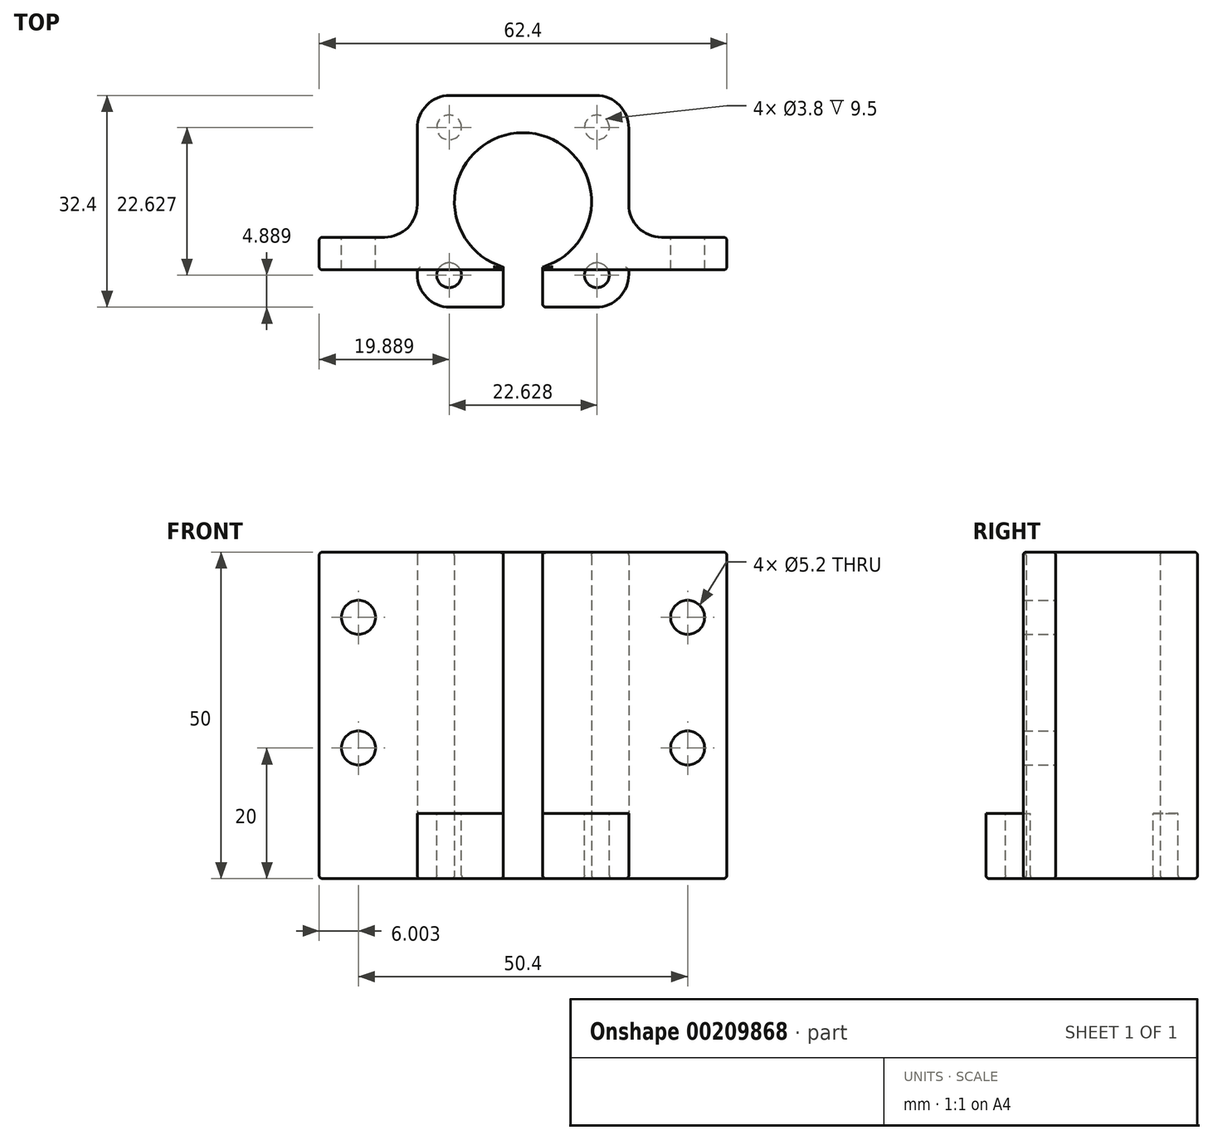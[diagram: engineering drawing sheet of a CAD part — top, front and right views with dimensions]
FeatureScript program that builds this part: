
annotation { "Feature Type Name" : "Feature", "Feature Type Description" : "" }
export const myFeature = defineFeature(function(context is Context, id is Id, definition is map)
    precondition{}
    {
        {
            var Q0;
            Q0=qCreatedBy(makeId("Top.planeOp"),FACE);
            var sketch = newSketch(context, id + "F0", { "sketchPlane" : qUnion([Q0])});
            skCircle(sketch, "E0", {"center": v(-42.16, 28.22) * mm, "radius": 6 * mm, "construction": true});
            skCircle(sketch, "E1", {"center": v(-42.16, 28.22) * mm, "radius": 16 * mm, "construction": true});
            skLineSegment(sketch, "E2.bottom", {"start": v(-58.36, 44.42) * mm, "end": v(-25.96, 44.42) * mm, "construction": true});
            skLineSegment(sketch, "E2.top", {"start": v(-58.36, 12.02) * mm, "end": v(-25.96, 12.02) * mm, "construction": true});
            skLineSegment(sketch, "E2.left", {"start": v(-58.36, 44.42) * mm, "end": v(-58.36, 12.02) * mm, "construction": true});
            skLineSegment(sketch, "E2.right", {"start": v(-25.96, 44.42) * mm, "end": v(-25.96, 12.02) * mm, "construction": true});
            skLineSegment(sketch, "E3", {"start": v(-58.36, 44.42) * mm, "end": v(-25.96, 12.02) * mm, "construction": true});
            skLineSegment(sketch, "E4", {"start": v(-58.36, 12.02) * mm, "end": v(-25.96, 44.42) * mm, "construction": true});
            skPoint(sketch, "E5", {"position": v(-53.47, 39.54) * mm});
            skPoint(sketch, "E6", {"position": v(-30.84, 39.54) * mm});
            skPoint(sketch, "E7", {"position": v(-30.84, 16.9) * mm});
            skPoint(sketch, "E8", {"position": v(-53.47, 16.9) * mm});
            skCircle(sketch, "E9", {"center": v(-42.16, 28.22) * mm, "radius": 10.5 * mm});
            skLineSegment(sketch, "E10.bottom", {"start": v(-58.36, 17.72) * mm, "end": v(-73.36, 17.72) * mm});
            skLineSegment(sketch, "E10.top", {"start": v(-58.36, 22.72) * mm, "end": v(-73.36, 22.72) * mm});
            skLineSegment(sketch, "E10.left", {"start": v(-58.36, 17.72) * mm, "end": v(-58.36, 22.72) * mm});
            skLineSegment(sketch, "E10.right", {"start": v(-73.36, 17.72) * mm, "end": v(-73.36, 22.72) * mm});
            skLineSegment(sketch, "E11.bottom", {"start": v(-25.96, 17.72) * mm, "end": v(-10.96, 17.72) * mm});
            skLineSegment(sketch, "E11.top", {"start": v(-25.96, 22.72) * mm, "end": v(-10.96, 22.72) * mm});
            skLineSegment(sketch, "E11.left", {"start": v(-25.96, 17.72) * mm, "end": v(-25.96, 22.72) * mm});
            skLineSegment(sketch, "E11.right", {"start": v(-10.96, 17.72) * mm, "end": v(-10.96, 22.72) * mm});
            skLineSegment(sketch, "E12.bottom", {"start": v(-58.36, 44.42) * mm, "end": v(-25.96, 44.42) * mm});
            skLineSegment(sketch, "E12.top", {"start": v(-58.36, 17.72) * mm, "end": v(-25.96, 17.72) * mm});
            skLineSegment(sketch, "E12.left", {"start": v(-58.36, 44.42) * mm, "end": v(-58.36, 17.72) * mm});
            skLineSegment(sketch, "E12.right", {"start": v(-25.96, 44.42) * mm, "end": v(-25.96, 17.72) * mm});
            skLineSegment(sketch, "E13.top", {"start": v(-58.36, 12.02) * mm, "end": v(-25.96, 12.02) * mm});
            skLineSegment(sketch, "E13.left", {"start": v(-58.36, 17.72) * mm, "end": v(-58.36, 12.02) * mm});
            skLineSegment(sketch, "E13.right", {"start": v(-25.96, 17.72) * mm, "end": v(-25.96, 12.02) * mm});
            skLineSegment(sketch, "E14", {"start": v(-39.16, 18.16) * mm, "end": v(-39.16, 12.02) * mm});
            skLineSegment(sketch, "E15", {"start": v(-45.16, 18.16) * mm, "end": v(-45.16, 12.02) * mm});
            skSolve(sketch);
        }
        {
            var Q0;
            {var subQ6=sQuery(id+"F0.wireOp",EDGE,"E10.left");Q0=makeQuery(id+"F0.imprint","IMPRINT",FACE,{"disambiguationData":[TD([[makeQuery(id+"F0.imprint","IMPRINT",EDGE,{"derivedFrom":subQ6}),-1.0]])]});}
            var Q1;
            Q1=makeQuery(id+"F0.imprint","IMPRINT",FACE,{"disambiguationData":[TD([[makeQuery(id+"F0.imprint","IMPRINT",EDGE,{"derivedFrom":sQuery(id+"F0.wireOp",EDGE,"E11.bottom")}),1.0]])]});
            var Q2;
            Q2=makeQuery(id+"F0.imprint","IMPRINT",FACE,{"disambiguationData":[TD([[makeQuery(id+"F0.imprint","IMPRINT",EDGE,{"derivedFrom":sQuery(id+"F0.wireOp",EDGE,"E10.bottom")}),-1.0]])]});
            extrude(context, id + "F1", {"entities" : qUnion([Q0, Q1, Q2]), "depth" : 40 * mm, "offsetDistance" : 25 * mm});
        }
        {
            var Q0;
            {var subQ6=sQuery(id+"F0.wireOp",EDGE,"E10.left");Q0=makeQuery(id+"F0.imprint","IMPRINT",FACE,{"disambiguationData":[TD([[makeQuery(id+"F0.imprint","IMPRINT",EDGE,{"derivedFrom":subQ6}),-1.0]])]});}
            var Q1;
            {var subQ0=sQuery(id+"F0.wireOp",EDGE,"E13.left");Q1=makeQuery(id+"F0.imprint","IMPRINT",FACE,{"disambiguationData":[TD([[makeQuery(id+"F0.imprint","IMPRINT",EDGE,{"derivedFrom":subQ0}),1.0]])]});}
            var Q2;
            {var subQ0=sQuery(id+"F0.wireOp",EDGE,"E13.right");Q2=makeQuery(id+"F0.imprint","IMPRINT",FACE,{"disambiguationData":[TD([[makeQuery(id+"F0.imprint","IMPRINT",EDGE,{"derivedFrom":subQ0}),-1.0]])]});}
            var Q3;
            Q3=makeQuery(id+"F0.imprint","IMPRINT",FACE,{"disambiguationData":[TD([[makeQuery(id+"F0.imprint","IMPRINT",EDGE,{"derivedFrom":sQuery(id+"F0.wireOp",EDGE,"E11.bottom")}),1.0]])]});
            var Q4;
            Q4=makeQuery(id+"F0.imprint","IMPRINT",FACE,{"disambiguationData":[TD([[makeQuery(id+"F0.imprint","IMPRINT",EDGE,{"derivedFrom":sQuery(id+"F0.wireOp",EDGE,"E10.bottom")}),-1.0]])]});
            extrude(context, id + "F2", {"entities" : qUnion([Q0, Q1, Q2, Q3, Q4]), "operationType" : NewBodyOperationType.ADD, "oppositeDirection" : true, "depth" : 10 * mm, "offsetDistance" : 25 * mm});
        }
        {
            var Q0;
            Q0=makeQuery(id+"F1.opExtrude","SWEPT_EDGE",EDGE,{"disambiguationData":[OSD([sQuery(id+"F0.wireOp",EDGE,"E10.top"),sQuery(id+"F0.wireOp",EDGE,"E10.left"),sQuery(id+"F0.wireOp",EDGE,"E12.left")])]});
            var Q1;
            {var subQ0=sQuery(id+"F0.wireOp",EDGE,"E12.left");var subQ1=sQuery(id+"F0.wireOp",EDGE,"E12.bottom");Q1=makeQuery(id+"F2.boolean.opBoolean","MERGE",EDGE,{"derivedFrom":[makeQuery(id+"F1.opExtrude","SWEPT_EDGE",EDGE,{"disambiguationData":[OSD([subQ1,subQ0])]}),makeQuery(id+"F2.opExtrude","SWEPT_EDGE",EDGE,{"disambiguationData":[OSD([subQ1,subQ0])]})]});}
            var Q2;
            {var subQ0=sQuery(id+"F0.wireOp",EDGE,"E12.right");var subQ1=sQuery(id+"F0.wireOp",EDGE,"E12.bottom");Q2=makeQuery(id+"F2.boolean.opBoolean","MERGE",EDGE,{"derivedFrom":[makeQuery(id+"F1.opExtrude","SWEPT_EDGE",EDGE,{"disambiguationData":[OSD([subQ1,subQ0])]}),makeQuery(id+"F2.opExtrude","SWEPT_EDGE",EDGE,{"disambiguationData":[OSD([subQ1,subQ0])]})]});}
            var Q3;
            Q3=makeQuery(id+"F1.opExtrude","SWEPT_EDGE",EDGE,{"disambiguationData":[OSD([sQuery(id+"F0.wireOp",EDGE,"E11.top"),sQuery(id+"F0.wireOp",EDGE,"E11.left"),sQuery(id+"F0.wireOp",EDGE,"E12.right")])]});
            var Q4;
            Q4=makeQuery(id+"F2.opExtrude","SWEPT_EDGE",EDGE,{"disambiguationData":[OSD([sQuery(id+"F0.wireOp",EDGE,"E13.top"),sQuery(id+"F0.wireOp",EDGE,"E13.right")])]});
            var Q5;
            Q5=makeQuery(id+"F2.opExtrude","SWEPT_EDGE",EDGE,{"disambiguationData":[OSD([sQuery(id+"F0.wireOp",EDGE,"E13.top"),sQuery(id+"F0.wireOp",EDGE,"E13.left")])]});
            fillet(context, id + "F3", {"entities" : qUnion([Q0, Q1, Q2, Q3, Q4, Q5]), "tangentPropagation" : true, "radius" : 5 * mm, "defaultsChanged" : false, "vertexSettings" : [], "allowEdgeOverflow" : false});
        }
        {
            var Q0;
            Q0=sQuery(id+"F0.wireOp",VERTEX,"E8");
            var Q1;
            Q1=sQuery(id+"F0.wireOp",VERTEX,"E7");
            var Q2;
            Q2=sQuery(id+"F0.wireOp",VERTEX,"E6");
            var Q3;
            Q3=sQuery(id+"F0.wireOp",VERTEX,"E5");
            var Q4;
            Q4=makeQuery(id+"F1.opExtrude","SWEPT_BODY",BODY,{"disambiguationData":[OSD([sQuery(id+"F0.wireOp",EDGE,"E9"),sQuery(id+"F0.wireOp",EDGE,"E10.bottom"),sQuery(id+"F0.wireOp",EDGE,"E10.top"),sQuery(id+"F0.wireOp",EDGE,"E10.right"),sQuery(id+"F0.wireOp",EDGE,"E11.bottom"),sQuery(id+"F0.wireOp",EDGE,"E11.top"),sQuery(id+"F0.wireOp",EDGE,"E11.right"),sQuery(id+"F0.wireOp",EDGE,"E12.bottom"),sQuery(id+"F0.wireOp",EDGE,"E12.top"),sQuery(id+"F0.wireOp",EDGE,"E12.left"),sQuery(id+"F0.wireOp",EDGE,"E12.right"),sQuery(id+"F0.wireOp",EDGE,"4NraLiJI-Y3Cm-em6W-jGHa-r2u25gr67TQr"),sQuery(id+"F0.wireOp",EDGE,"sMZY98dh-ObRl-6XGD-h9oM-HqnPOMrwm9us")])]});
            hole(context, id + "F4", {"style" : HoleStyle.SIMPLE, "endStyle" : HoleEndStyle.BLIND, "holeDiameter" : 3.8 * mm, "majorDiameter" : 5 * mm, "holeDepth" : 10 * mm, "isTappedThrough" : true, "tappedDepth" : 12 * mm, "tapClearance" : 3, "locations" : qUnion([Q0, Q1, Q2, Q3]), "scope" : qUnion([Q4])});
        }
        {
            var Q0;
            {var subQ0=sQuery(id+"F0.wireOp",EDGE,"E11.top");Q0=makeQuery(id+"F2.boolean.opBoolean","MERGE",FACE,{"derivedFrom":[makeQuery(id+"F1.opExtrude","SWEPT_FACE",FACE,{"disambiguationData":[OSD([subQ0])]}),makeQuery(id+"F2.opExtrude","SWEPT_FACE",FACE,{"disambiguationData":[OSD([subQ0])]})]});}
            var sketch = newSketch(context, id + "F5", { "sketchPlane" : qUnion([Q0])});
            skPoint(sketch, "E16", {"position": v(16.96, 30) * mm});
            skPoint(sketch, "E17", {"position": v(16.96, 10) * mm});
            skPoint(sketch, "E18", {"position": v(67.36, 30) * mm});
            skPoint(sketch, "E19", {"position": v(67.36, 10) * mm});
            skSolve(sketch);
        }
        {
            var Q0;
            Q0=sQuery(id+"F5.wireOp",VERTEX,"E16");
            var Q1;
            Q1=sQuery(id+"F5.wireOp",VERTEX,"E17");
            var Q2;
            Q2=sQuery(id+"F5.wireOp",VERTEX,"E18");
            var Q3;
            Q3=sQuery(id+"F5.wireOp",VERTEX,"E19");
            var Q4;
            Q4=makeQuery(id+"F1.opExtrude","SWEPT_BODY",BODY,{"disambiguationData":[OSD([sQuery(id+"F0.wireOp",EDGE,"E9"),sQuery(id+"F0.wireOp",EDGE,"E10.bottom"),sQuery(id+"F0.wireOp",EDGE,"E10.top"),sQuery(id+"F0.wireOp",EDGE,"E10.right"),sQuery(id+"F0.wireOp",EDGE,"E11.bottom"),sQuery(id+"F0.wireOp",EDGE,"E11.top"),sQuery(id+"F0.wireOp",EDGE,"E11.right"),sQuery(id+"F0.wireOp",EDGE,"E12.bottom"),sQuery(id+"F0.wireOp",EDGE,"E12.top"),sQuery(id+"F0.wireOp",EDGE,"E12.left"),sQuery(id+"F0.wireOp",EDGE,"E12.right"),sQuery(id+"F0.wireOp",EDGE,"4NraLiJI-Y3Cm-em6W-jGHa-r2u25gr67TQr"),sQuery(id+"F0.wireOp",EDGE,"sMZY98dh-ObRl-6XGD-h9oM-HqnPOMrwm9us")])]});
            hole(context, id + "F6", {"style" : HoleStyle.SIMPLE, "endStyle" : HoleEndStyle.BLIND, "holeDiameter" : 5.2 * mm, "majorDiameter" : 5 * mm, "holeDepth" : 10 * mm, "isTappedThrough" : true, "tappedDepth" : 12 * mm, "tapClearance" : 3, "locations" : qUnion([Q0, Q1, Q2, Q3]), "scope" : qUnion([Q4])});
        }
        {
            var Q0;
            Q0=makeQuery(id+"F2.opExtrude","CAP_FACE",FACE,{"disambiguationData":[OSD([sQuery(id+"F0.wireOp",EDGE,"E9"),sQuery(id+"F0.wireOp",EDGE,"E10.bottom"),sQuery(id+"F0.wireOp",EDGE,"E10.top"),sQuery(id+"F0.wireOp",EDGE,"E10.right"),sQuery(id+"F0.wireOp",EDGE,"E11.bottom"),sQuery(id+"F0.wireOp",EDGE,"E11.top"),sQuery(id+"F0.wireOp",EDGE,"E11.right"),sQuery(id+"F0.wireOp",EDGE,"E12.bottom"),sQuery(id+"F0.wireOp",EDGE,"E12.left"),sQuery(id+"F0.wireOp",EDGE,"E12.right"),sQuery(id+"F0.wireOp",EDGE,"4NraLiJI-Y3Cm-em6W-jGHa-r2u25gr67TQr"),sQuery(id+"F0.wireOp",EDGE,"sMZY98dh-ObRl-6XGD-h9oM-HqnPOMrwm9us"),sQuery(id+"F0.wireOp",EDGE,"E13.top"),sQuery(id+"F0.wireOp",EDGE,"E13.left"),sQuery(id+"F0.wireOp",EDGE,"E13.right"),sQuery(id+"F0.wireOp",EDGE,"ejsexS8x-yKEw-zrY8-fCX2-bjoYlObCuS4N"),sQuery(id+"F0.wireOp",EDGE,"oZpC30q2-KvE7-LrhN-lm9K-tZZtgmLt5vyO")])],"isStart":false});
            var Q1;
            {var subQ0=sQuery(id+"F0.wireOp",EDGE,"E10.right");Q1=makeQuery(id+"F2.boolean.opBoolean","MERGE",FACE,{"derivedFrom":[makeQuery(id+"F1.opExtrude","SWEPT_FACE",FACE,{"disambiguationData":[OSD([subQ0])]}),makeQuery(id+"F2.opExtrude","SWEPT_FACE",FACE,{"disambiguationData":[OSD([subQ0])]})]});}
            var Q2;
            Q2=makeQuery(id+"F1.opExtrude","CAP_FACE",FACE,{"disambiguationData":[OSD([sQuery(id+"F0.wireOp",EDGE,"E9"),sQuery(id+"F0.wireOp",EDGE,"E10.bottom"),sQuery(id+"F0.wireOp",EDGE,"E10.top"),sQuery(id+"F0.wireOp",EDGE,"E10.right"),sQuery(id+"F0.wireOp",EDGE,"E11.bottom"),sQuery(id+"F0.wireOp",EDGE,"E11.top"),sQuery(id+"F0.wireOp",EDGE,"E11.right"),sQuery(id+"F0.wireOp",EDGE,"E12.bottom"),sQuery(id+"F0.wireOp",EDGE,"E12.top"),sQuery(id+"F0.wireOp",EDGE,"E12.left"),sQuery(id+"F0.wireOp",EDGE,"E12.right"),sQuery(id+"F0.wireOp",EDGE,"4NraLiJI-Y3Cm-em6W-jGHa-r2u25gr67TQr"),sQuery(id+"F0.wireOp",EDGE,"sMZY98dh-ObRl-6XGD-h9oM-HqnPOMrwm9us")])],"isStart":false});
            var Q3;
            {var subQ0=sQuery(id+"F0.wireOp",EDGE,"E11.right");Q3=makeQuery(id+"F2.boolean.opBoolean","MERGE",FACE,{"derivedFrom":[makeQuery(id+"F1.opExtrude","SWEPT_FACE",FACE,{"disambiguationData":[OSD([subQ0])]}),makeQuery(id+"F2.opExtrude","SWEPT_FACE",FACE,{"disambiguationData":[OSD([subQ0])]})]});}
            var Q4;
            Q4=makeQuery(id+"F2.opExtrude","SWEPT_EDGE",EDGE,{"disambiguationData":[OSD([sQuery(id+"F0.wireOp",EDGE,"E13.top"),sQuery(id+"F0.wireOp",EDGE,"oZpC30q2-KvE7-LrhN-lm9K-tZZtgmLt5vyO")])]});
            var Q5;
            Q5=makeQuery(id+"F2.opExtrude","SWEPT_EDGE",EDGE,{"disambiguationData":[OSD([sQuery(id+"F0.wireOp",EDGE,"E13.top"),sQuery(id+"F0.wireOp",EDGE,"ejsexS8x-yKEw-zrY8-fCX2-bjoYlObCuS4N")])]});
            var Q6;
            Q6=makeQuery(id+"F2.opExtrude","CAP_EDGE",EDGE,{"disambiguationData":[OSD([sQuery(id+"F0.wireOp",EDGE,"sMZY98dh-ObRl-6XGD-h9oM-HqnPOMrwm9us"),sQuery(id+"F0.wireOp",EDGE,"oZpC30q2-KvE7-LrhN-lm9K-tZZtgmLt5vyO")])],"isStart":true});
            var Q7;
            Q7=makeQuery(id+"F2.opExtrude","CAP_EDGE",EDGE,{"disambiguationData":[OSD([sQuery(id+"F0.wireOp",EDGE,"4NraLiJI-Y3Cm-em6W-jGHa-r2u25gr67TQr"),sQuery(id+"F0.wireOp",EDGE,"ejsexS8x-yKEw-zrY8-fCX2-bjoYlObCuS4N")])],"isStart":true});
            fillet(context, id + "F7", {"entities" : qUnion([Q0, Q1, Q2, Q3, Q4, Q5, Q6, Q7]), "tangentPropagation" : true, "radius" : 0.5 * mm, "defaultsChanged" : false, "vertexSettings" : [], "allowEdgeOverflow" : false});
        }
    });
